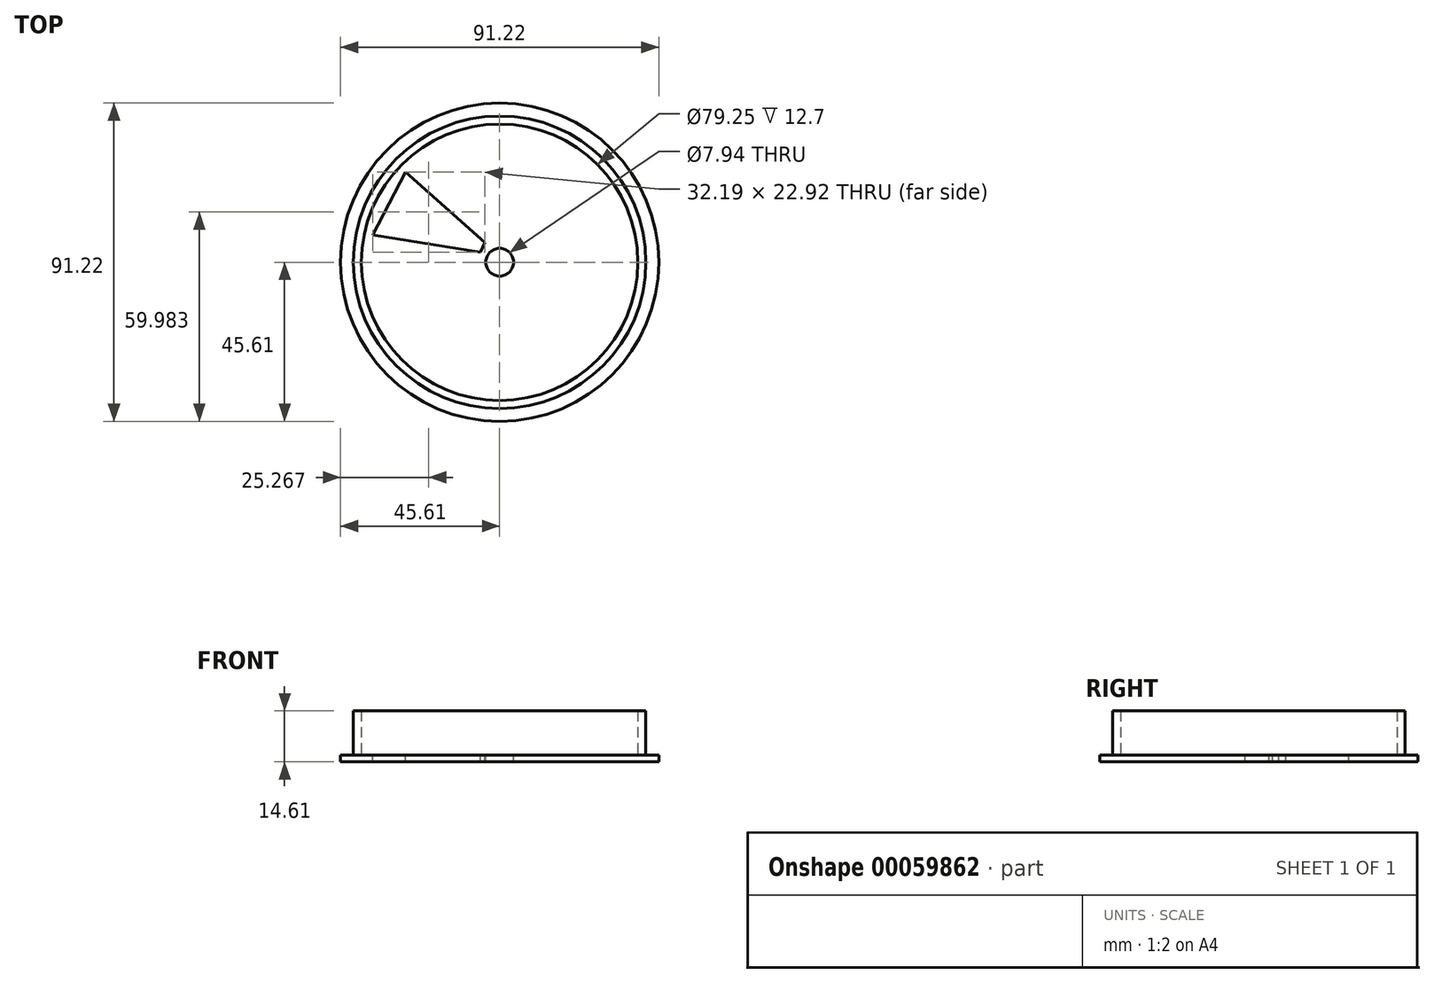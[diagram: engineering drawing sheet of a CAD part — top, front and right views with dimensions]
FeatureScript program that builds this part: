
annotation { "Feature Type Name" : "Feature", "Feature Type Description" : "" }
export const myFeature = defineFeature(function(context is Context, id is Id, definition is map)
    precondition{}
    {
        {
            var Q0;
            Q0=qCreatedBy(makeId("Top.planeOp"),FACE);
            var sketch = newSketch(context, id + "F0", { "sketchPlane" : qUnion([Q0])});
            skCircle(sketch, "E0", {"center": v(0, 0) * mm, "radius": 39.62 * mm});
            skCircle(sketch, "E1", {"center": v(0, 0) * mm, "radius": 41.91 * mm});
            skSolve(sketch);
        }
        {
            var Q0;
            Q0 = qSketchRegion(id + "F0", true);
            extrude(context, id + "F1", {"entities" : qUnion([Q0]), "depth" : 12.7 * mm});
        }
        {
            var Q0;
            Q0=qCreatedBy(makeId("Top.planeOp"),FACE);
            var sketch = newSketch(context, id + "F2", { "sketchPlane" : qUnion([Q0])});
            skCircle(sketch, "E2", {"center": v(0, 0) * mm, "radius": 45.6 * mm});
            skSolve(sketch);
        }
        {
            var Q0;
            Q0=qCreatedBy(makeId("Top.planeOp"),FACE);
            var sketch = newSketch(context, id + "F3", { "sketchPlane" : qUnion([Q0])});
            skCircle(sketch, "E3", {"center": v(0, 0) * mm, "radius": 3.97 * mm});
            skSolve(sketch);
        }
        {
            var Q0;
            Q0 = qSketchRegion(id + "F2", true);
            extrude(context, id + "F4", {"entities" : qUnion([Q0]), "operationType" : NewBodyOperationType.ADD, "oppositeDirection" : true, "depth" : 1.9 * mm});
        }
        {
            var Q0;
            Q0 = qSketchRegion(id + "F3", true);
            extrude(context, id + "F5", {"entities" : qUnion([Q0]), "operationType" : NewBodyOperationType.REMOVE, "oppositeDirection" : true, "depth" : 25.4 * mm});
        }
        {
            var Q0;
            Q0=qCreatedBy(makeId("Top.planeOp"),FACE);
            var sketch = newSketch(context, id + "F6", { "sketchPlane" : qUnion([Q0])});
            skLineSegment(sketch, "E4", {"start": v(-4.25, 5.67) * mm, "end": v(-26.96, 25.83) * mm});
            skLineSegment(sketch, "E5", {"start": v(-26.96, 25.83) * mm, "end": v(-36.44, 7.8) * mm});
            skLineSegment(sketch, "E6", {"start": v(-36.44, 7.8) * mm, "end": v(-5.48, 2.92) * mm});
            skLineSegment(sketch, "E7", {"start": v(-5.48, 2.92) * mm, "end": v(-4.25, 5.67) * mm});
            skSolve(sketch);
        }
        {
            var Q0;
            Q0 = qSketchRegion(id + "F6", true);
            extrude(context, id + "F7", {"entities" : qUnion([Q0]), "operationType" : NewBodyOperationType.REMOVE, "oppositeDirection" : true, "depth" : 5.33 * mm});
        }
    });
